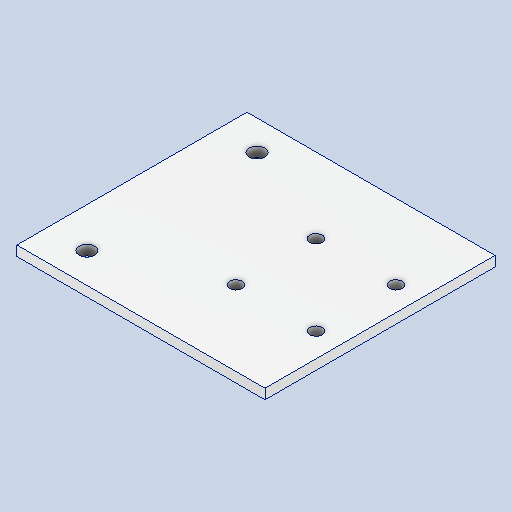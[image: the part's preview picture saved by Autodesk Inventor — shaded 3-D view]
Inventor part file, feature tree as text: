
AUTODESK INVENTOR PART (.ipt)
format: ipt  version: 2023 (Build 270158000, 158)  size: 155,648 bytes
history: native  units: in
note: dims shown in document units (in); Inventor stores cm internally (conversion verified against a paired STEP export)
features: extrude x3, sketch x2, projected_geometry x1
ambient origin geometry x8: Origin, YZ Plane, XZ Plane, XY Plane, X Axis, Y Axis, Z Axis, Center Point
bodies: Solid1 (feature_tree)
feature tree (6):
  extrude  "Extrusion1"  Depth=1.875in
  sketch  "Sketch2"  dims[d2=0.1969in d3=0.1969in d4=0.5in d5=0.5in d6=0.375in d7=0.375in d8=1.0in d9=1.0in d10=1.0in d11=1.0in d12=0.159in d13=0.159in d14=0.159in d15=0.159in d16=0.4375in d17=0.125in d18=0.0in d19=3.1in d20=0.375in d21=0.5in d22=0.5in d23=0.375in d24=0.5in d25=0.5in d26=0.125in d27=0.0in d28=0.0in d29=0.0in]
  extrude  "Extrusion2"  Depth=0.125in
  extrude  "Extrusion3"  Depth=0.125in
  sketch  "Sketch1"  dims[d0=4.0in d1=1.875in]
  projected_geometry  "Projected Loop1"
